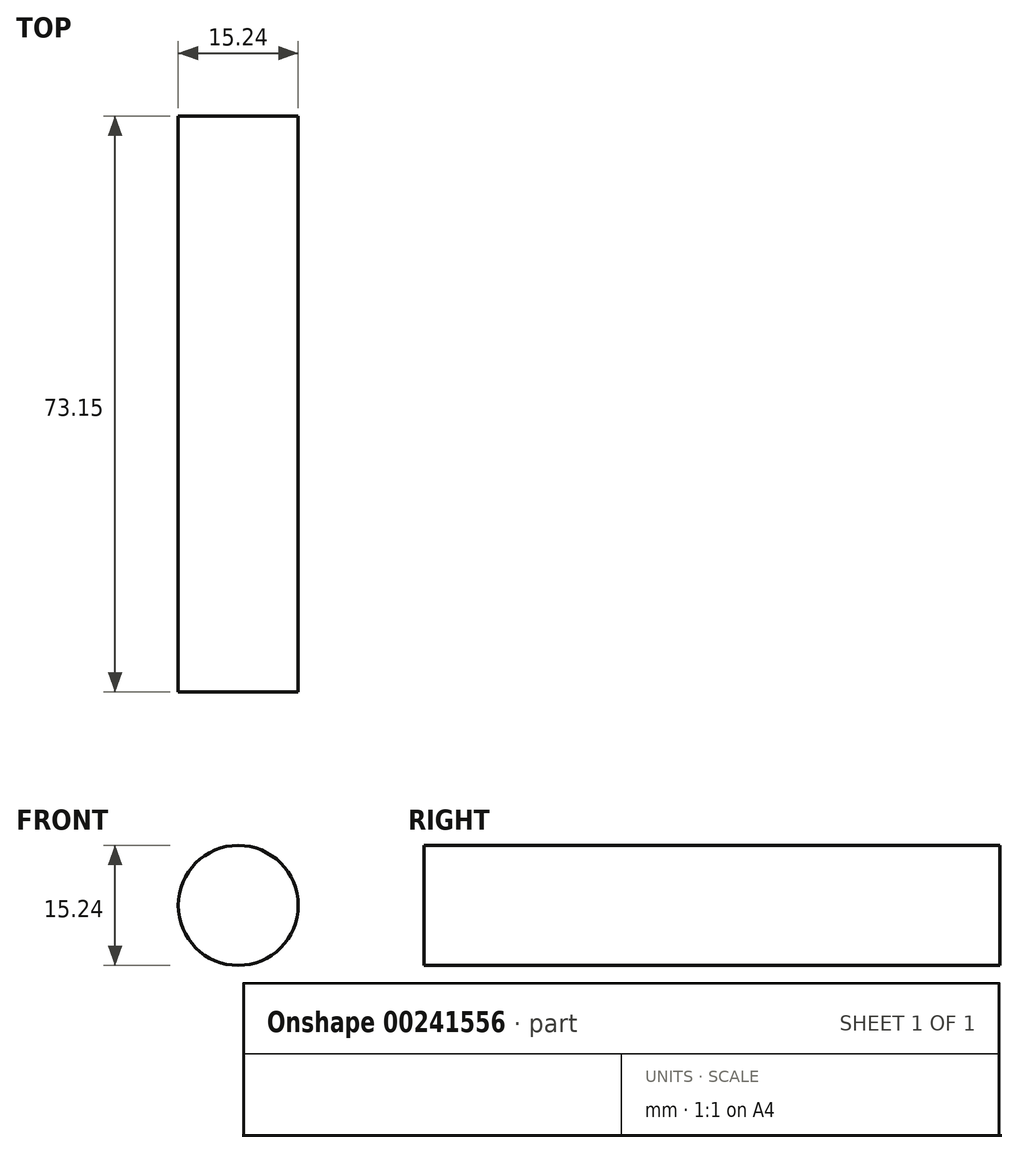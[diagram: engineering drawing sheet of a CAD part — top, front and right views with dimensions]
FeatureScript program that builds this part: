
annotation { "Feature Type Name" : "Feature", "Feature Type Description" : "" }
export const myFeature = defineFeature(function(context is Context, id is Id, definition is map)
    precondition{}
    {
        {
            var Q0;
            Q0=qCreatedBy(makeId("Front.planeOp"),FACE);
            var sketch = newSketch(context, id + "F0", { "sketchPlane" : qUnion([Q0])});
            skCircle(sketch, "E0", {"center": v(0, 0) * mm, "radius": 7.62 * mm});
            skSolve(sketch);
        }
        {
            var Q0;
            Q0 = qSketchRegion(id + "F0", true);
            extrude(context, id + "F1", {"entities" : qUnion([Q0]), "depth" : 73.15 * mm});
        }
    });
